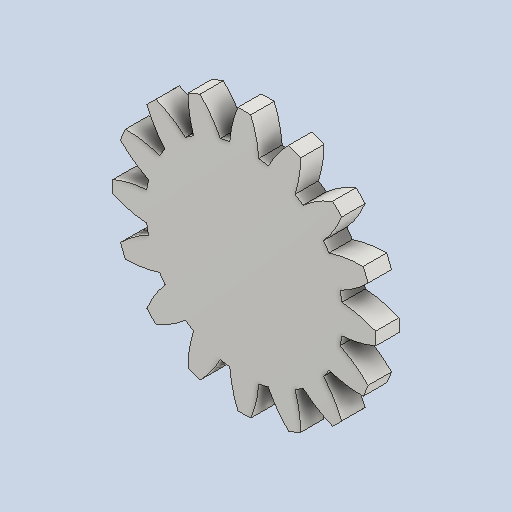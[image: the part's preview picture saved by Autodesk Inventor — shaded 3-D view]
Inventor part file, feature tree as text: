
AUTODESK INVENTOR PART (.ipt)
format: ipt  version: 2025 (Build 290162010, 162A)  size: 211,968 bytes
history: native  units: mm (DEFAULTED — no unit token found)
features: plane x3, other x3, extrude x1, sketch x1
ambient origin geometry x8: Origin, YZ Plane, XZ Plane, XY Plane, X Axis, Y Axis, Z Axis, Center Point
bodies: Solid1 (feature_tree)
feature tree (8):
  extrude  "Extrusion1"  Depth=20.0mm TaperAngle=0.0deg
  plane  "Work Plane2"
  plane  "Work Plane8"
  plane  "Work Plane9"
  other  "Spur Gear"
  sketch  "Sketch1"  dims[d0=225.0mm d1=20.0mm d2=0.0mm d3=200.0mm d4=10.0mm d5=0.0mm d16=700.0mm d17=0.0mm d34=1.963495mm d39=0.0mm d41=0.0mm d43=700.0mm d46=700.0mm d47=0.0mm d48=0.0mm]
  other  "Srf1"
  other  "Pitch Diameter"
